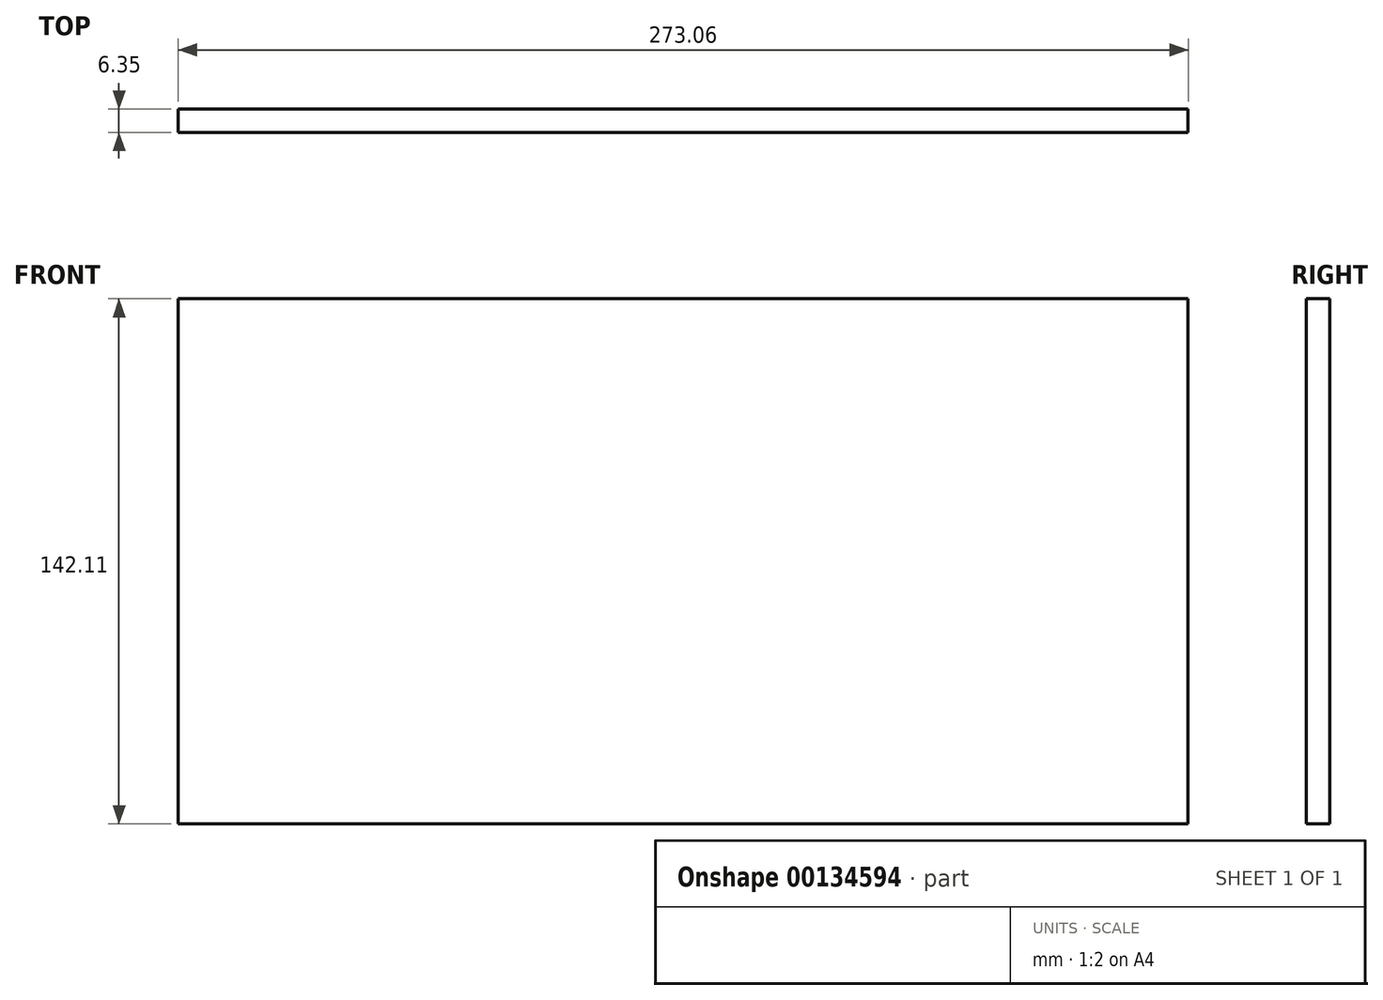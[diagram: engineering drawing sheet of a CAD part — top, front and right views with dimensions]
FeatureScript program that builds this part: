
annotation { "Feature Type Name" : "Feature", "Feature Type Description" : "" }
export const myFeature = defineFeature(function(context is Context, id is Id, definition is map)
    precondition{}
    {
        {
            var Q0;
            Q0=qCreatedBy(makeId("Front.planeOp"),FACE);
            var sketch = newSketch(context, id + "F0", { "sketchPlane" : qUnion([Q0])});
            skLineSegment(sketch, "E0.top", {"start": v(-136.52, -65.91) * mm, "end": v(136.53, -65.91) * mm});
            skLineSegment(sketch, "E0.left", {"start": v(-136.52, 76.2) * mm, "end": v(-136.52, -65.91) * mm});
            skLineSegment(sketch, "E0.right", {"start": v(136.53, 76.2) * mm, "end": v(136.53, -65.91) * mm});
            skPoint(sketch, "E1", {"position": v(0, 0) * mm});
            skPoint(sketch, "E2", {"position": v(0, -65.91) * mm});
            skLineSegment(sketch, "E3", {"start": v(-136.52, 76.2) * mm, "end": v(136.53, 76.2) * mm});
            skSolve(sketch);
        }
        {
            var Q0;
            Q0=qSketchRegion(id+"F0",true);
            extrude(context, id + "F1", {"entities" : qUnion([Q0]), "depth" : 6.35 * mm});
        }
        {
            var Q0;
            Q0 = qSketchRegion(id + "F0", true);
            extrude(context, id + "F2", {"entities" : qUnion([Q0]), "operationType" : NewBodyOperationType.ADD, "depth" : 6.35 * mm});
        }
    });
